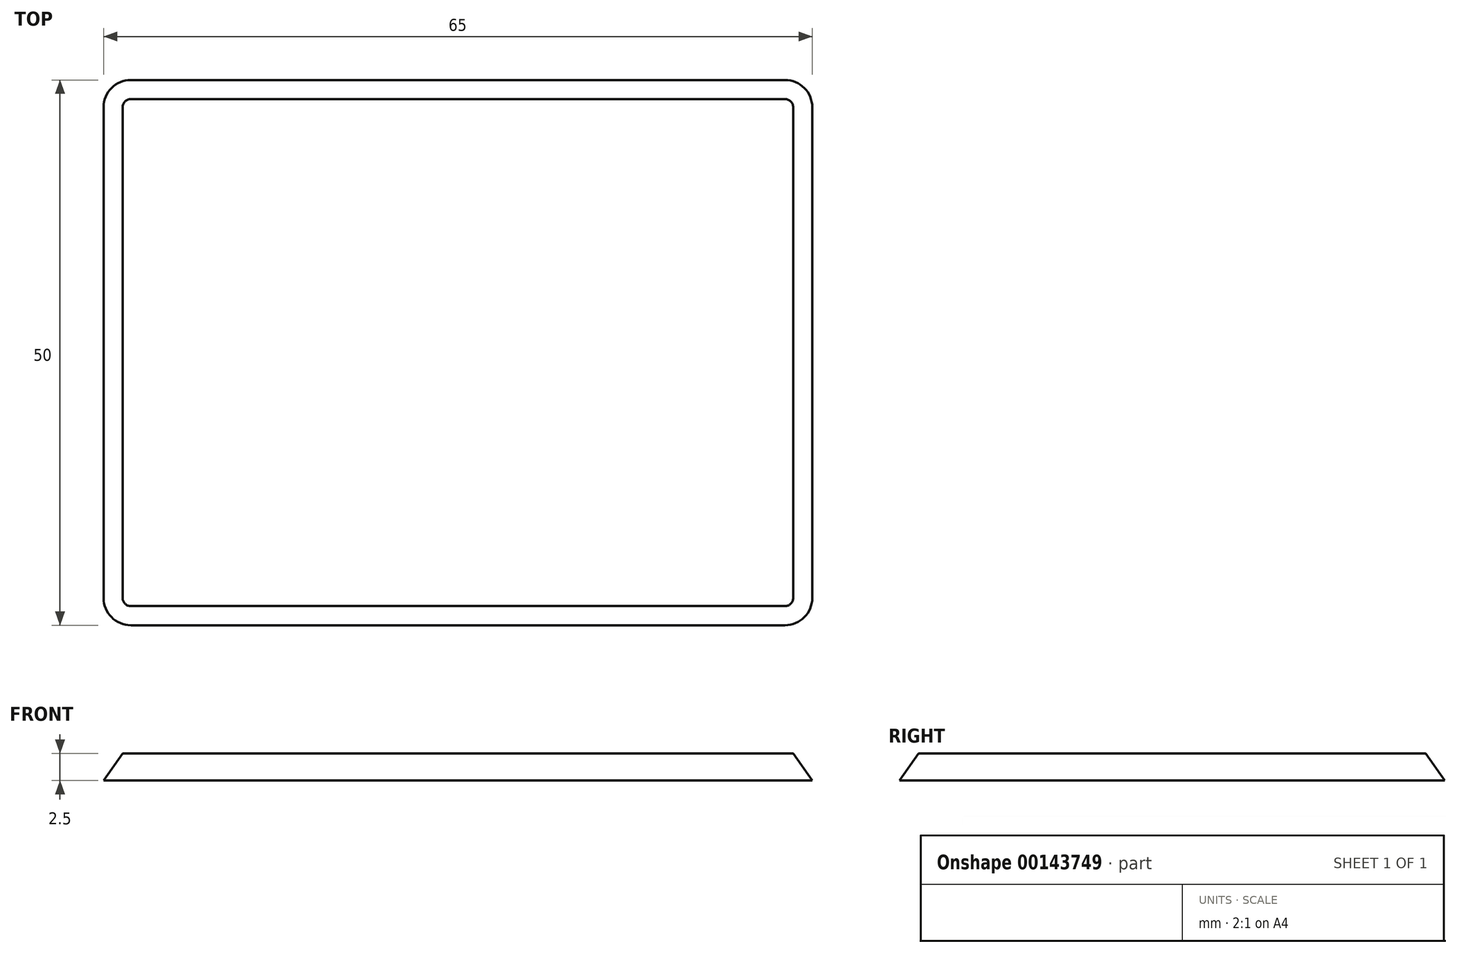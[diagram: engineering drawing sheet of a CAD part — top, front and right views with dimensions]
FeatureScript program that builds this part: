
annotation { "Feature Type Name" : "Feature", "Feature Type Description" : "" }
export const myFeature = defineFeature(function(context is Context, id is Id, definition is map)
    precondition{}
    {
        {
            var Q0;
            Q0=qCreatedBy(makeId("Top.planeOp"),FACE);
            var sketch = newSketch(context, id + "F0", { "sketchPlane" : qUnion([Q0])});
            skLineSegment(sketch, "E0.bottom", {"start": v(-32.5, 25) * mm, "end": v(32.5, 25) * mm});
            skLineSegment(sketch, "E0.top", {"start": v(-32.5, -25) * mm, "end": v(32.5, -25) * mm});
            skLineSegment(sketch, "E0.left", {"start": v(-32.5, 25) * mm, "end": v(-32.5, -25) * mm});
            skLineSegment(sketch, "E0.right", {"start": v(32.5, 25) * mm, "end": v(32.5, -25) * mm});
            skPoint(sketch, "E0.middle", {"position": v(0, 0) * mm});
            skSolve(sketch);
        }
        {
            var Q0;
            Q0=makeQuery(id+"F0.imprint","IMPRINT",FACE,{"disambiguationData":[TD([[makeQuery(id+"F0.imprint","IMPRINT",EDGE,{"derivedFrom":sQuery(id+"F0.wireOp",EDGE,"E0.bottom")}),-1.0]])]});
            extrude(context, id + "F1", {"entities" : qUnion([Q0]), "depth" : 2.5 * mm});
        }
        {
            var Q0;
            Q0=makeQuery(id+"F1.opExtrude","SWEPT_EDGE",EDGE,{"disambiguationData":[OSD([sQuery(id+"F0.wireOp",EDGE,"E0.top"),sQuery(id+"F0.wireOp",EDGE,"E0.left")])]});
            var Q1;
            Q1=makeQuery(id+"F1.opExtrude","SWEPT_EDGE",EDGE,{"disambiguationData":[OSD([sQuery(id+"F0.wireOp",EDGE,"E0.top"),sQuery(id+"F0.wireOp",EDGE,"E0.right")])]});
            var Q2;
            Q2=makeQuery(id+"F1.opExtrude","SWEPT_EDGE",EDGE,{"disambiguationData":[OSD([sQuery(id+"F0.wireOp",EDGE,"E0.bottom"),sQuery(id+"F0.wireOp",EDGE,"E0.right")])]});
            var Q3;
            Q3=makeQuery(id+"F1.opExtrude","SWEPT_EDGE",EDGE,{"disambiguationData":[OSD([sQuery(id+"F0.wireOp",EDGE,"E0.bottom"),sQuery(id+"F0.wireOp",EDGE,"E0.left")])]});
            fillet(context, id + "F2", {"entities" : qUnion([Q0, Q1, Q2, Q3]), "radius" : 2.5 * mm, "tangentPropagation" : true, "allowEdgeOverflow" : false});
        }
        {
            var Q0;
            Q0=makeQuery(id+"F1.opExtrude","CAP_EDGE",EDGE,{"disambiguationData":[OSD([sQuery(id+"F0.wireOp",EDGE,"E0.left")])],"isStart":false});
            var Q1;
            {var subQ0=sQuery(id+"F0.wireOp",EDGE,"E0.left");var subQ1=sQuery(id+"F0.wireOp",EDGE,"E0.bottom");Q1=makeQuery(id+"F2.opFillet","BLEND_EDGE",EDGE,{"blendedFrom":[makeQuery(id+"F1.opExtrude","SWEPT_EDGE",EDGE,{"disambiguationData":[OSD([subQ1,subQ0])]}),makeQuery(id+"F1.opExtrude","CAP_FACE",FACE,{"disambiguationData":[OSD([subQ1,sQuery(id+"F0.wireOp",EDGE,"E0.top"),subQ0,sQuery(id+"F0.wireOp",EDGE,"E0.right")])],"isStart":false})],"blendedInto":[makeQuery(id+"F1.opExtrude","CAP_FACE",FACE,{"disambiguationData":[OSD([subQ1,sQuery(id+"F0.wireOp",EDGE,"E0.top"),subQ0,sQuery(id+"F0.wireOp",EDGE,"E0.right")])],"isStart":false})]});}
            var Q2;
            Q2=makeQuery(id+"F1.opExtrude","CAP_EDGE",EDGE,{"disambiguationData":[OSD([sQuery(id+"F0.wireOp",EDGE,"E0.bottom")])],"isStart":false});
            var Q3;
            {var subQ0=sQuery(id+"F0.wireOp",EDGE,"E0.right");var subQ1=sQuery(id+"F0.wireOp",EDGE,"E0.bottom");Q3=makeQuery(id+"F2.opFillet","BLEND_EDGE",EDGE,{"blendedFrom":[makeQuery(id+"F1.opExtrude","SWEPT_EDGE",EDGE,{"disambiguationData":[OSD([subQ1,subQ0])]}),makeQuery(id+"F1.opExtrude","CAP_FACE",FACE,{"disambiguationData":[OSD([subQ1,sQuery(id+"F0.wireOp",EDGE,"E0.top"),sQuery(id+"F0.wireOp",EDGE,"E0.left"),subQ0])],"isStart":false})],"blendedInto":[makeQuery(id+"F1.opExtrude","CAP_FACE",FACE,{"disambiguationData":[OSD([subQ1,sQuery(id+"F0.wireOp",EDGE,"E0.top"),sQuery(id+"F0.wireOp",EDGE,"E0.left"),subQ0])],"isStart":false})]});}
            var Q4;
            Q4=makeQuery(id+"F1.opExtrude","CAP_EDGE",EDGE,{"disambiguationData":[OSD([sQuery(id+"F0.wireOp",EDGE,"E0.right")])],"isStart":false});
            var Q5;
            {var subQ0=sQuery(id+"F0.wireOp",EDGE,"E0.right");var subQ1=sQuery(id+"F0.wireOp",EDGE,"E0.top");Q5=makeQuery(id+"F2.opFillet","BLEND_EDGE",EDGE,{"blendedFrom":[makeQuery(id+"F1.opExtrude","SWEPT_EDGE",EDGE,{"disambiguationData":[OSD([subQ1,subQ0])]}),makeQuery(id+"F1.opExtrude","CAP_FACE",FACE,{"disambiguationData":[OSD([sQuery(id+"F0.wireOp",EDGE,"E0.bottom"),subQ1,sQuery(id+"F0.wireOp",EDGE,"E0.left"),subQ0])],"isStart":false})],"blendedInto":[makeQuery(id+"F1.opExtrude","CAP_FACE",FACE,{"disambiguationData":[OSD([sQuery(id+"F0.wireOp",EDGE,"E0.bottom"),subQ1,sQuery(id+"F0.wireOp",EDGE,"E0.left"),subQ0])],"isStart":false})]});}
            var Q6;
            Q6=makeQuery(id+"F1.opExtrude","CAP_EDGE",EDGE,{"disambiguationData":[OSD([sQuery(id+"F0.wireOp",EDGE,"E0.top")])],"isStart":false});
            var Q7;
            {var subQ0=sQuery(id+"F0.wireOp",EDGE,"E0.left");var subQ1=sQuery(id+"F0.wireOp",EDGE,"E0.top");Q7=makeQuery(id+"F2.opFillet","BLEND_EDGE",EDGE,{"blendedFrom":[makeQuery(id+"F1.opExtrude","SWEPT_EDGE",EDGE,{"disambiguationData":[OSD([subQ1,subQ0])]}),makeQuery(id+"F1.opExtrude","CAP_FACE",FACE,{"disambiguationData":[OSD([sQuery(id+"F0.wireOp",EDGE,"E0.bottom"),subQ1,subQ0,sQuery(id+"F0.wireOp",EDGE,"E0.right")])],"isStart":false})],"blendedInto":[makeQuery(id+"F1.opExtrude","CAP_FACE",FACE,{"disambiguationData":[OSD([sQuery(id+"F0.wireOp",EDGE,"E0.bottom"),subQ1,subQ0,sQuery(id+"F0.wireOp",EDGE,"E0.right")])],"isStart":false})]});}
            chamfer(context, id + "F3", {"entities" : qUnion([Q0, Q1, Q2, Q3, Q4, Q5, Q6, Q7]), "chamferType" : ChamferType.OFFSET_ANGLE, "width" : 2.5 * mm, "oppositeDirection" : true, "angle" : 35 * degree, "tangentPropagation" : true});
        }
    });
